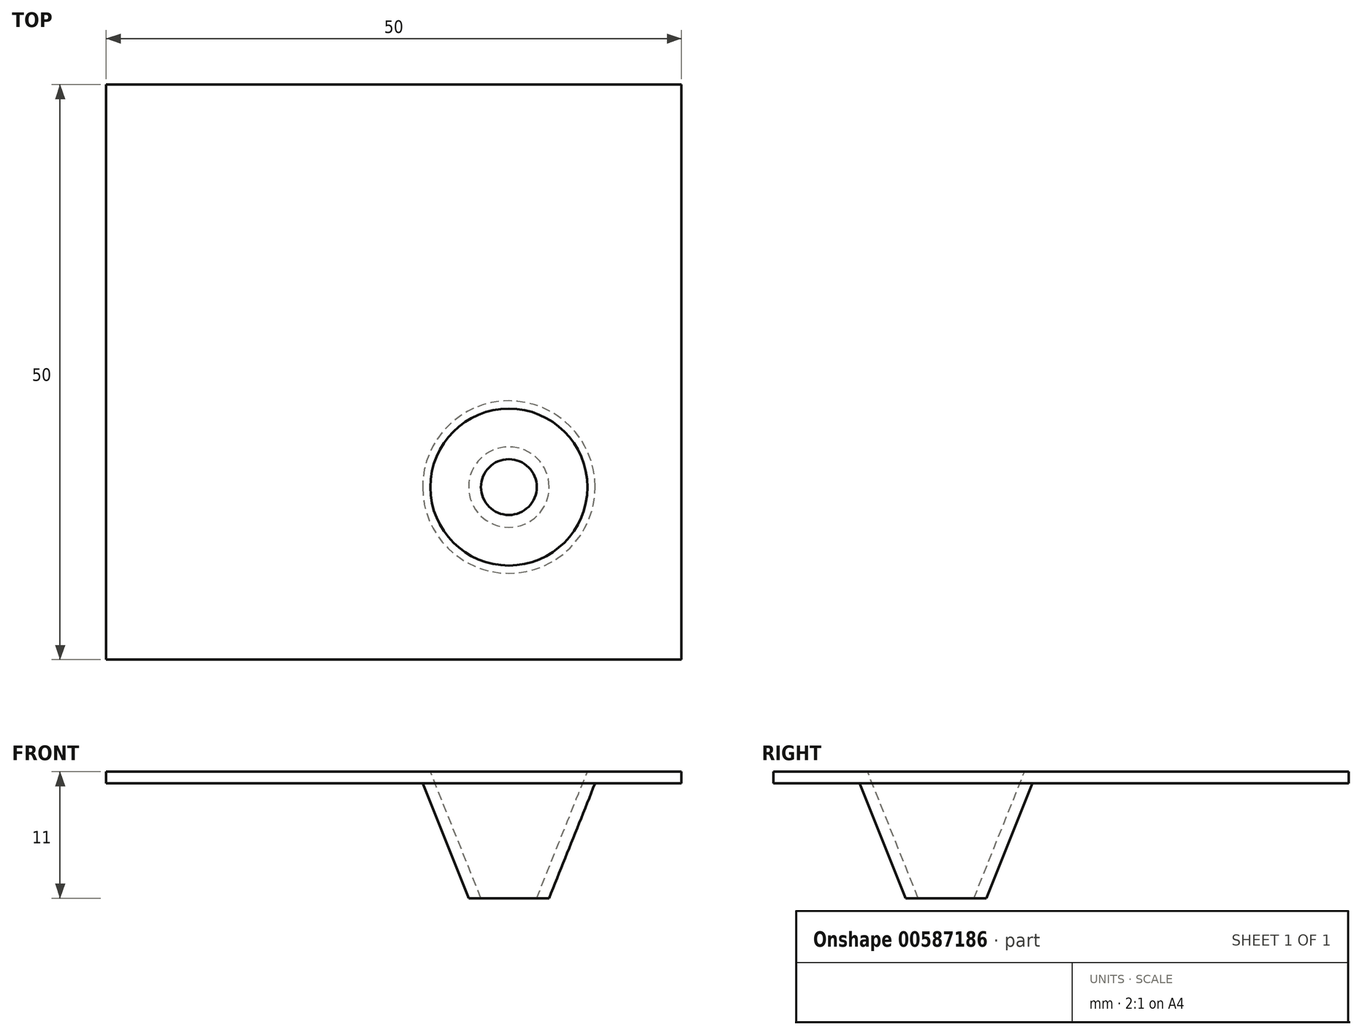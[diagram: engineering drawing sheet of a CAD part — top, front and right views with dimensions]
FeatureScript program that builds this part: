
annotation { "Feature Type Name" : "Feature", "Feature Type Description" : "" }
export const myFeature = defineFeature(function(context is Context, id is Id, definition is map)
    precondition{}
    {
        {
            var Q0;
            Q0=qCreatedBy(makeId("Top.planeOp"),FACE);
            var sketch = newSketch(context, id + "F0", { "sketchPlane" : qUnion([Q0])});
            skLineSegment(sketch, "E0.bottom", {"start": v(25, -25) * mm, "end": v(-25, -25) * mm});
            skLineSegment(sketch, "E0.top", {"start": v(25, 25) * mm, "end": v(-25, 25) * mm});
            skLineSegment(sketch, "E0.left", {"start": v(25, -25) * mm, "end": v(25, 25) * mm});
            skLineSegment(sketch, "E0.right", {"start": v(-25, -25) * mm, "end": v(-25, 25) * mm});
            skPoint(sketch, "E0.middle", {"position": v(0, 0) * mm});
            skSolve(sketch);
        }
        {
            var Q0;
            Q0=makeQuery(id+"F0.imprint","IMPRINT",FACE,{"disambiguationData":[TD([[makeQuery(id+"F0.imprint","IMPRINT",EDGE,{"derivedFrom":sQuery(id+"F0.wireOp",EDGE,"E0.bottom")}),-1.0]])]});
            extrude(context, id + "F1", {"entities" : qUnion([Q0]), "depth" : 1 * mm, "offsetDistance" : 25 * mm});
        }
        {
            var Q0;
            Q0=makeQuery(id+"F1.opExtrude","CAP_FACE",FACE,{"disambiguationData":[OSD([sQuery(id+"F0.wireOp",EDGE,"E0.bottom"),sQuery(id+"F0.wireOp",EDGE,"E0.top"),sQuery(id+"F0.wireOp",EDGE,"E0.left"),sQuery(id+"F0.wireOp",EDGE,"E0.right")])],"isStart":true});
            var sketch = newSketch(context, id + "F2", { "sketchPlane" : qUnion([Q0])});
            skCircle(sketch, "E1", {"center": v(10, 10) * mm, "radius": 7.5 * mm});
            skSolve(sketch);
        }
        {
            var Q0;
            Q0=qCreatedBy(makeId("Top.planeOp"),FACE);
            cPlane(context, id + "F3", {"entities" : qUnion([Q0]), "cplaneType" : CPlaneType.OFFSET, "offset" : 10 * mm, "oppositeDirection" : true, "width" : 150 * mm, "height" : 150 * mm});
        }
        {
            var Q0;
            Q0=qCreatedBy(id+"F3.planeOp",FACE);
            var sketch = newSketch(context, id + "F4", { "sketchPlane" : qUnion([Q0])});
            skCircle(sketch, "E2", {"center": v(10, -10) * mm, "radius": 3.5 * mm});
            skSolve(sketch);
        }
        {
            var Q1;
            Q1=makeQuery(id+"F2.imprint","IMPRINT",FACE,{"disambiguationData":[TD([[makeQuery(id+"F2.imprint","IMPRINT",EDGE,{"derivedFrom":sQuery(id+"F2.wireOp",EDGE,"E1")}),1.0]])]});
            var Q2;
            Q2=makeQuery(id+"F4.imprint","IMPRINT",FACE,{"disambiguationData":[TD([[makeQuery(id+"F4.imprint","IMPRINT",EDGE,{"derivedFrom":sQuery(id+"F4.wireOp",EDGE,"E2")}),1.0]])]});
            loft(context, id + "F5", {"operationType" : NewBodyOperationType.ADD, "sheetProfilesArray" : [{ "sheetProfileEntities" : qUnion([Q1]) }, { "sheetProfileEntities" : qUnion([Q2]) }]});
        }
        {
            var Q0;
            Q0=makeQuery(id+"F1.opExtrude","CAP_FACE",FACE,{"disambiguationData":[OSD([sQuery(id+"F0.wireOp",EDGE,"E0.bottom"),sQuery(id+"F0.wireOp",EDGE,"E0.top"),sQuery(id+"F0.wireOp",EDGE,"E0.left"),sQuery(id+"F0.wireOp",EDGE,"E0.right")])],"isStart":false});
            var Q1;
            Q1=makeQuery(id+"F5.opLoft","CAP_FACE",FACE,{"disambiguationData":[OSD([makeQuery(id+"F4.imprint","IMPRINT",FACE,{"disambiguationData":[TD([[makeQuery(id+"F4.imprint","IMPRINT",EDGE,{"derivedFrom":sQuery(id+"F4.wireOp",EDGE,"E2")}),1.0]])]})])],"isStart":true});
            shell(context, id + "F6", {"entities" : qUnion([Q0, Q1]), "thickness" : 1 * mm});
        }
    });
